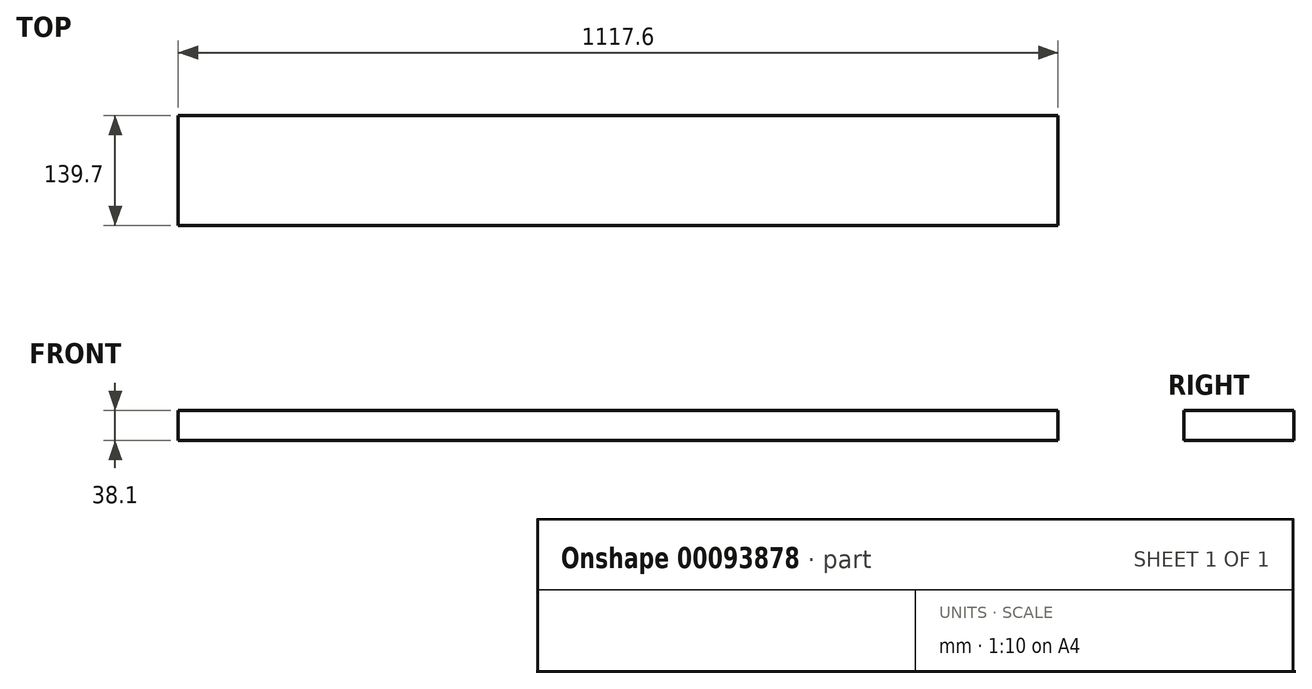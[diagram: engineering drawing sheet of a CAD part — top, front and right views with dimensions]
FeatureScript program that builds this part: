
annotation { "Feature Type Name" : "Feature", "Feature Type Description" : "" }
export const myFeature = defineFeature(function(context is Context, id is Id, definition is map)
    precondition{}
    {
        {
            var Q0;
            Q0=qCreatedBy(makeId("Top.planeOp"),FACE);
            var sketch = newSketch(context, id + "F0", { "sketchPlane" : qUnion([Q0])});
            skLineSegment(sketch, "E0.bottom", {"start": v(-558.8, 139.7) * mm, "end": v(558.8, 139.7) * mm});
            skLineSegment(sketch, "E0.top", {"start": v(-558.8, 0) * mm, "end": v(558.8, 0) * mm});
            skLineSegment(sketch, "E0.left", {"start": v(-558.8, 139.7) * mm, "end": v(-558.8, 0) * mm});
            skLineSegment(sketch, "E0.right", {"start": v(558.8, 139.7) * mm, "end": v(558.8, 0) * mm});
            skSolve(sketch);
        }
        {
            var Q0;
            Q0=qSketchRegion(id+"F0",true);
            extrude(context, id + "F1", {"entities" : qUnion([Q0]), "depth" : 38.1 * mm});
        }
    });
